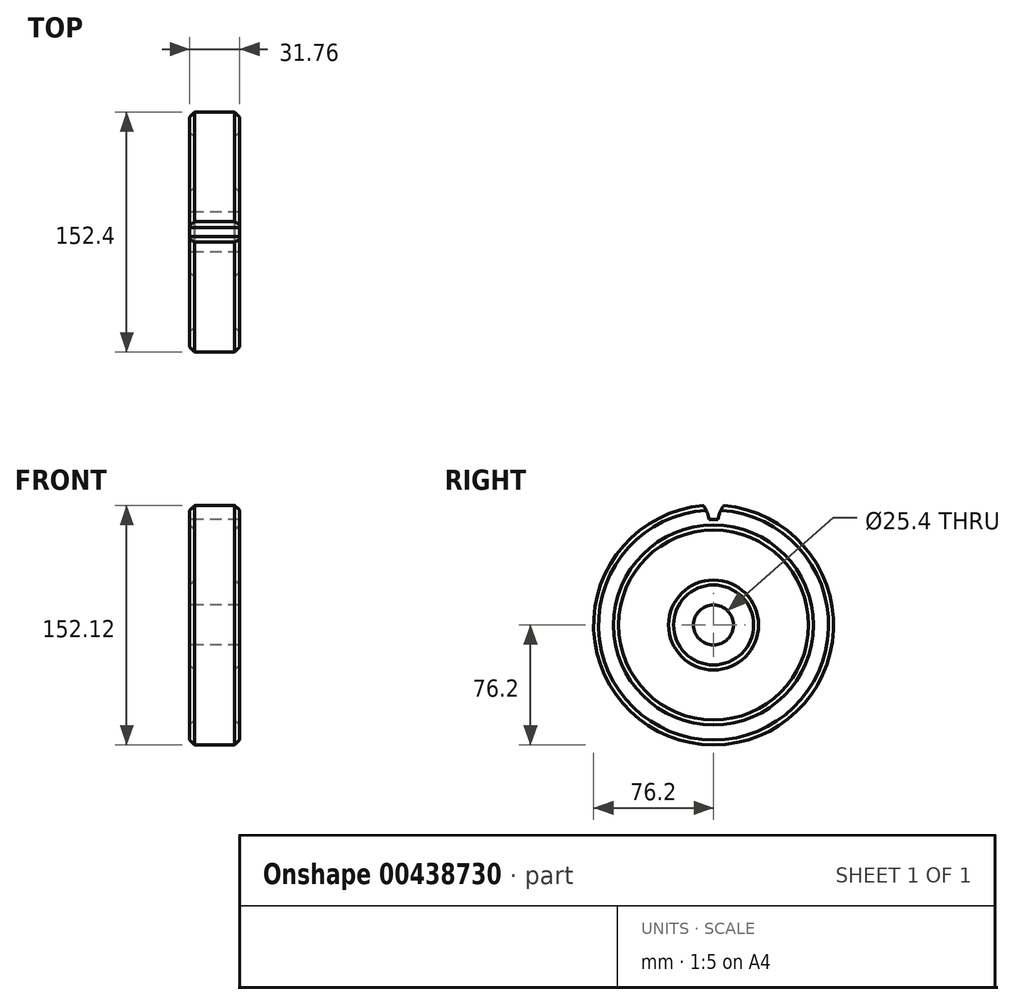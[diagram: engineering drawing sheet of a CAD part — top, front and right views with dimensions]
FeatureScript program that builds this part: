
annotation { "Feature Type Name" : "Feature", "Feature Type Description" : "" }
export const myFeature = defineFeature(function(context is Context, id is Id, definition is map)
    precondition{}
    {
        {
            var Q0;
            Q0=qCreatedBy(makeId("Front.planeOp"),FACE);
            var sketch = newSketch(context, id + "F0", { "sketchPlane" : qUnion([Q0])});
            skLineSegment(sketch, "E0", {"start": v(0, 0) * mm, "end": v(0, 63.5) * mm});
            skLineSegment(sketch, "E1", {"start": v(0, 63.5) * mm, "end": v(12.7, 63.5) * mm});
            skLineSegment(sketch, "E2", {"start": v(12.7, 63.5) * mm, "end": v(15.88, 60.32) * mm});
            skLineSegment(sketch, "E3", {"start": v(15.88, 60.32) * mm, "end": v(15.88, 50.8) * mm});
            skLineSegment(sketch, "E4", {"start": v(15.88, 50.8) * mm, "end": v(12.7, 47.62) * mm});
            skLineSegment(sketch, "E5", {"start": v(12.7, 47.62) * mm, "end": v(12.7, 15.88) * mm});
            skLineSegment(sketch, "E6", {"start": v(12.7, 15.88) * mm, "end": v(15.88, 12.7) * mm});
            skLineSegment(sketch, "E7", {"start": v(15.88, 12.7) * mm, "end": v(15.88, 0) * mm});
            skLineSegment(sketch, "E8", {"start": v(15.87, 0) * mm, "end": v(0, 0) * mm});
            skLineSegment(sketch, "E9", {"start": v(0, 0) * mm, "end": v(0, -12.7) * mm});
            skLineSegment(sketch, "E10", {"start": v(0, -12.7) * mm, "end": v(14.91, -12.7) * mm});
            skLineSegment(sketch, "E11.MirrorCS", {"start": v(0, 63.5) * mm, "end": v(-12.7, 63.5) * mm});
            skLineSegment(sketch, "E12.MirrorCS", {"start": v(-15.88, 0) * mm, "end": v(0, 0) * mm});
            skLineSegment(sketch, "E13.MirrorCS", {"start": v(-15.88, 50.8) * mm, "end": v(-12.7, 47.62) * mm});
            skLineSegment(sketch, "E14.MirrorCS", {"start": v(-12.7, 63.5) * mm, "end": v(-15.88, 60.32) * mm});
            skLineSegment(sketch, "E15.MirrorCS", {"start": v(-12.7, 15.88) * mm, "end": v(-15.88, 12.7) * mm});
            skLineSegment(sketch, "E16.MirrorCS", {"start": v(-15.88, 12.7) * mm, "end": v(-15.88, 0) * mm});
            skLineSegment(sketch, "E17.MirrorCS", {"start": v(-15.88, 60.32) * mm, "end": v(-15.88, 50.8) * mm});
            skLineSegment(sketch, "E18.MirrorCS", {"start": v(-12.7, 47.62) * mm, "end": v(-12.7, 15.88) * mm});
            skSolve(sketch);
        }
        {
            var Q0;
            Q0=makeQuery(id+"F0.imprint","IMPRINT",FACE,{"disambiguationData":[TD([[makeQuery(id+"F0.imprint","IMPRINT",EDGE,{"derivedFrom":sQuery(id+"F0.wireOp",EDGE,"E0")}),-1.0]])]});
            var Q1;
            Q1=makeQuery(id+"F0.imprint","IMPRINT",FACE,{"disambiguationData":[TD([[makeQuery(id+"F0.imprint","IMPRINT",EDGE,{"derivedFrom":sQuery(id+"F0.wireOp",EDGE,"E0")}),1.0]])]});
            var Q2;
            Q2=sQuery(id+"F0.wireOp",EDGE,"E10");
            revolve(context, id + "F1", {"entities" : qUnion([Q0, Q1]), "axis" : qUnion([Q2]), "revolveType" : RevolveType.FULL});
        }
        {
            var Q0;
            Q0=makeQuery(id+"F1.opRevolve","SWEPT_FACE",FACE,{"disambiguationData":[OSD([sQuery(id+"F0.wireOp",EDGE,"E17.MirrorCS")])]});
            var sketch = newSketch(context, id + "F2", { "sketchPlane" : qUnion([Q0])});
            skLineSegment(sketch, "E19", {"start": v(0, -12.7) * mm, "end": v(0, 86.84) * mm});
            skLineSegment(sketch, "E20", {"start": v(0, 54.23) * mm, "end": v(2.86, 54.23) * mm});
            skArc(sketch, "E21", {"start": v(6.54, 63.22) * mm, "mid": v(4.12, 58.96) * mm, "end": v(2.86, 54.23) * mm});
            skLineSegment(sketch, "E22.MirrorCS", {"start": v(0, 54.23) * mm, "end": v(-2.86, 54.23) * mm});
            skArc(sketch, "E23.MirrorCS", {"start": v(-6.54, 63.22) * mm, "mid": v(-4.12, 58.96) * mm, "end": v(-2.86, 54.23) * mm});
            skArc(sketch, "E24.0", {"start": v(6.54, 63.22) * mm, "mid": v(0, 63.5) * mm, "end": v(-6.54, 63.22) * mm});
            skSolve(sketch);
        }
        {
            var Q0;
            {var subQ0=sQuery(id+"F2.wireOp",EDGE,"E24.0");var subQ5=sQuery(id+"F2.wireOp",EDGE,"E23.MirrorCS");var subQ6=makeQuery(id+"F2.imprint","INTERSECT",VERTEX,{"derivedFrom":[subQ5,subQ0]});Q0=makeQuery(id+"F2.imprint","IMPRINT",FACE,{"disambiguationData":[TD([[makeQuery(id+"F2.imprint","IMPRINT",EDGE,{"disambiguationData":[TD([[subQ6,1.0]])],"derivedFrom":subQ0}),1.0]])]});}
            var Q1;
            {var subQ0=sQuery(id+"F2.wireOp",EDGE,"E22.MirrorCS");Q1=makeQuery(id+"F2.imprint","IMPRINT",FACE,{"disambiguationData":[TD([[makeQuery(id+"F2.imprint","IMPRINT",EDGE,{"derivedFrom":subQ0}),-1.0]])]});}
            var Q2;
            {var subQ0=sQuery(id+"F2.wireOp",EDGE,"E20");Q2=makeQuery(id+"F2.imprint","IMPRINT",FACE,{"disambiguationData":[TD([[makeQuery(id+"F2.imprint","IMPRINT",EDGE,{"derivedFrom":subQ0}),1.0]])]});}
            var Q3;
            {var subQ0=sQuery(id+"F2.wireOp",EDGE,"E24.0");var subQ5=sQuery(id+"F2.wireOp",EDGE,"E21");var subQ6=makeQuery(id+"F2.imprint","INTERSECT",VERTEX,{"derivedFrom":[subQ5,subQ0]});Q3=makeQuery(id+"F2.imprint","IMPRINT",FACE,{"disambiguationData":[TD([[makeQuery(id+"F2.imprint","IMPRINT",EDGE,{"disambiguationData":[TD([[subQ6,-1.0]])],"derivedFrom":subQ0}),1.0]])]});}
            extrude(context, id + "F3", {"entities" : qUnion([Q0, Q1, Q2, Q3]), "operationType" : NewBodyOperationType.REMOVE, "endBound" : BoundingType.THROUGH_ALL, "oppositeDirection" : true, "depth" : 25.4 * mm});
        }
    });
